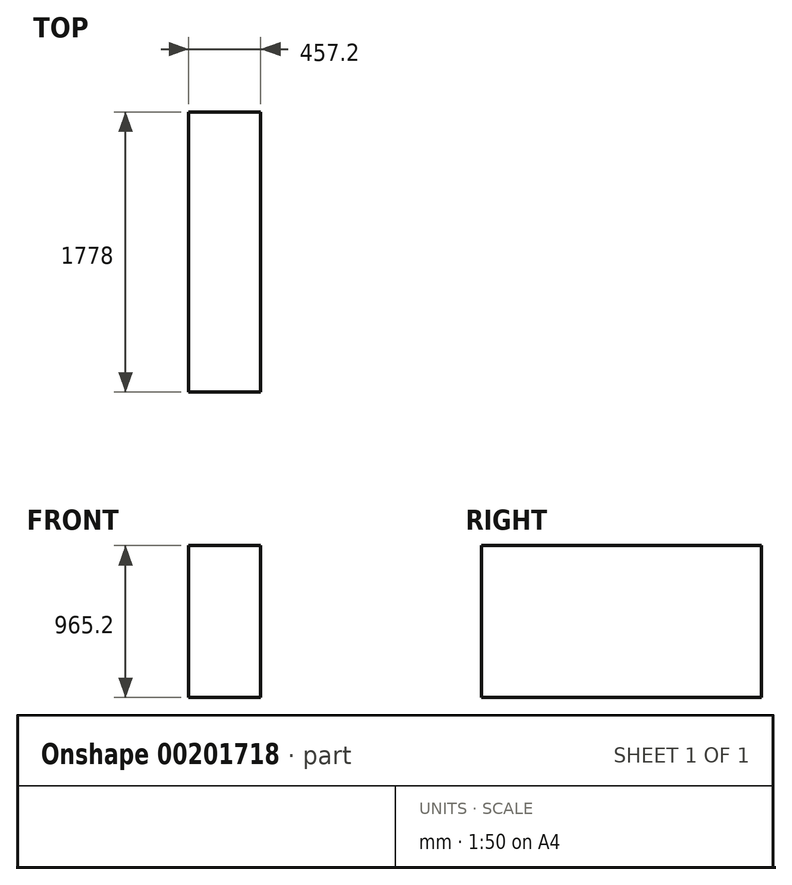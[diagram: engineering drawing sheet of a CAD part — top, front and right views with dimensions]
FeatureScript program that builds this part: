
annotation { "Feature Type Name" : "Feature", "Feature Type Description" : "" }
export const myFeature = defineFeature(function(context is Context, id is Id, definition is map)
    precondition{}
    {
        {
            var Q0;
            Q0=qCreatedBy(makeId("Top.planeOp"),FACE);
            var sketch = newSketch(context, id + "F0", { "sketchPlane" : qUnion([Q0])});
            skLineSegment(sketch, "E0.bottom", {"start": v(-228.6, 889) * mm, "end": v(228.6, 889) * mm});
            skLineSegment(sketch, "E0.top", {"start": v(-228.6, -889) * mm, "end": v(228.6, -889) * mm});
            skLineSegment(sketch, "E0.left", {"start": v(-228.6, 889) * mm, "end": v(-228.6, -889) * mm});
            skLineSegment(sketch, "E0.right", {"start": v(228.6, 889) * mm, "end": v(228.6, -889) * mm});
            skPoint(sketch, "E0.middle", {"position": v(0, 0) * mm});
            skSolve(sketch);
        }
        {
            var Q0;
            Q0 = qSketchRegion(id + "F0", true);
            extrude(context, id + "F1", {"entities" : qUnion([Q0]), "depth" : 965.2 * mm});
        }
    });
